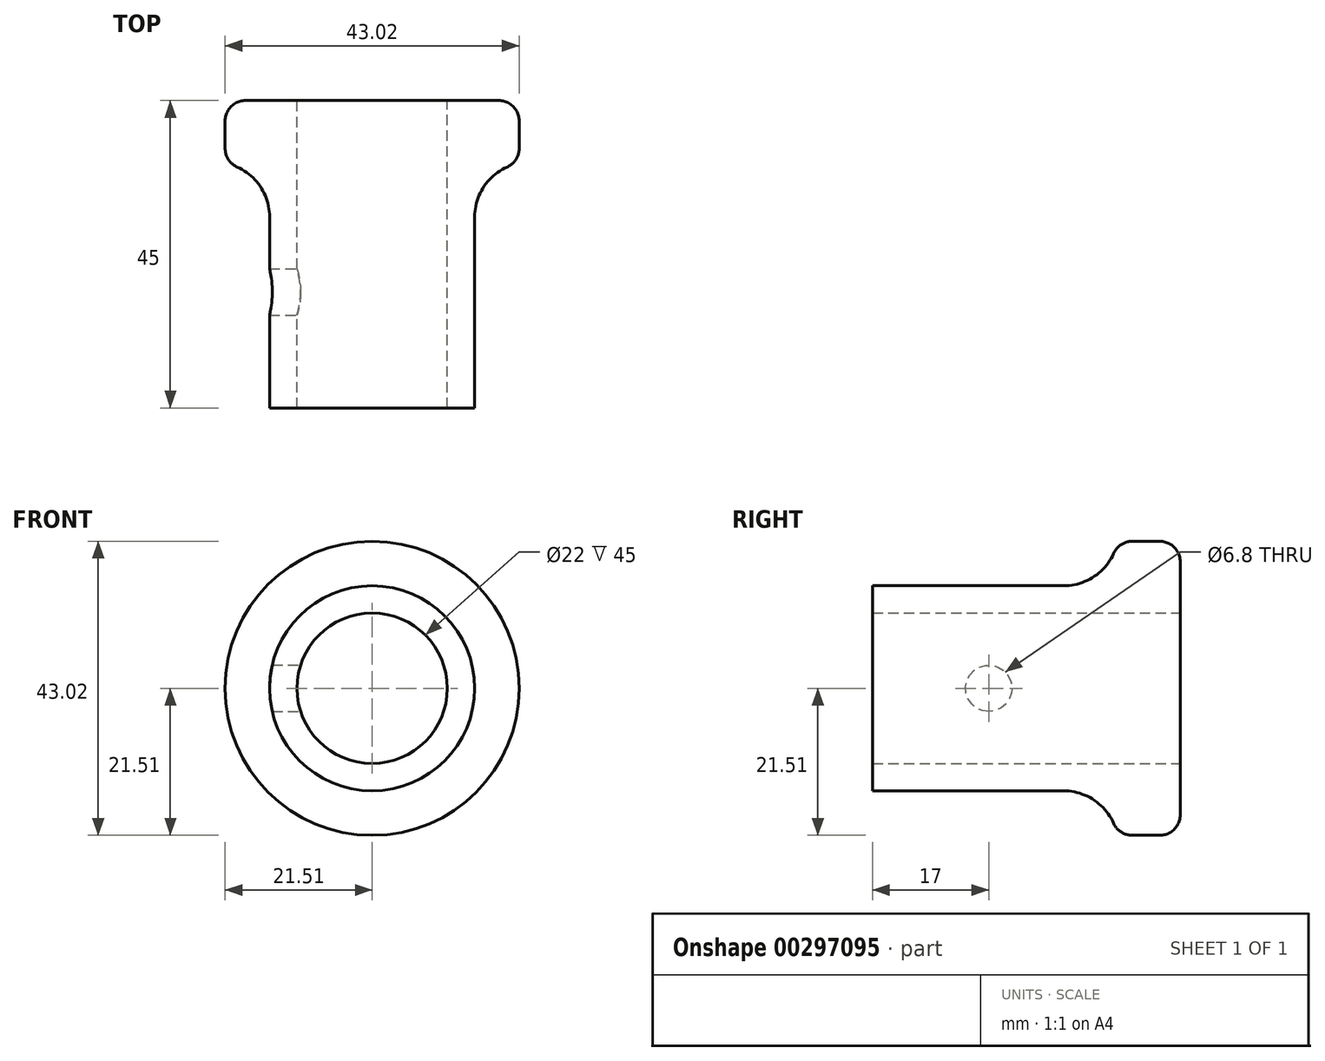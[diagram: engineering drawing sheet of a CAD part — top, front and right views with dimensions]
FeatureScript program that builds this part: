
annotation { "Feature Type Name" : "Feature", "Feature Type Description" : "" }
export const myFeature = defineFeature(function(context is Context, id is Id, definition is map)
    precondition{}
    {
        {
            var Q0;
            Q0=qCreatedBy(makeId("Front.planeOp"),FACE);
            var sketch = newSketch(context, id + "F0", { "sketchPlane" : qUnion([Q0])});
            skCircle(sketch, "E0", {"center": v(0, 0) * mm, "radius": 15 * mm});
            skSolve(sketch);
        }
        {
            var Q0;
            Q0 = qSketchRegion(id + "F0", true);
            extrude(context, id + "F1", {"entities" : qUnion([Q0]), "depth" : 45 * mm});
        }
        {
            var Q0;
            Q0=qCreatedBy(makeId("Front.planeOp"),FACE);
            var sketch = newSketch(context, id + "F2", { "sketchPlane" : qUnion([Q0])});
            skCircle(sketch, "E1", {"center": v(0, 0) * mm, "radius": 21.51 * mm});
            skSolve(sketch);
        }
        {
            var Q0;
            Q0=makeQuery(id+"F2.imprint","IMPRINT",FACE,{"disambiguationData":[TD([[makeQuery(id+"F2.imprint","IMPRINT",EDGE,{"derivedFrom":sQuery(id+"F2.wireOp",EDGE,"E1")}),1.0]])]});
            extrude(context, id + "F3", {"entities" : qUnion([Q0]), "operationType" : NewBodyOperationType.ADD, "depth" : 10 * mm});
        }
        {
            var Q0;
            Q0=sQuery(id+"F0.wireOp",VERTEX,"E0.center");
            var Q1;
            Q1=makeQuery(id+"F1.opExtrude","SWEPT_BODY",BODY,{"disambiguationData":[OSD([sQuery(id+"F0.wireOp",EDGE,"E0")])]});
            hole(context, id + "F4", {"style" : HoleStyle.SIMPLE, "endStyle" : HoleEndStyle.THROUGH, "oppositeDirection" : true, "holeDiameter" : 22 * mm, "tappedDepth" : 12.7 * mm, "tapClearance" : 3, "locations" : qUnion([Q0]), "scope" : qUnion([Q1])});
        }
        {
            var Q0;
            Q0=qCreatedBy(makeId("Right.planeOp"),FACE);
            var sketch = newSketch(context, id + "F5", { "sketchPlane" : qUnion([Q0])});
            skPoint(sketch, "E2", {"position": v(-28, 0) * mm});
            skPoint(sketch, "E3", {"position": v(-28, -20.88) * mm});
            skSolve(sketch);
        }
        {
            var Q0;
            Q0=sQuery(id+"F5.wireOp",VERTEX,"E2");
            var Q1;
            Q1=makeQuery(id+"F1.opExtrude","SWEPT_BODY",BODY,{"disambiguationData":[OSD([sQuery(id+"F0.wireOp",EDGE,"E0")])]});
            hole(context, id + "F6", {"style" : HoleStyle.SIMPLE, "endStyle" : HoleEndStyle.THROUGH, "standardTappedOrClearance" : lookupTablePath({ "standard" : "ISO", "engagement" : "75%", "pitch" : "1.25 mm", "size" : "M8", "type" : "Tapped" }), "standardBlindInLast" : lookupTablePath({ "standard" : "ISO", "engagement" : "75%", "pitch" : "1.25 mm", "size" : "M8", "type" : "Tapped" }), "holeDiameter" : 6.8 * mm, "showTappedDepth" : true, "tappedDepth" : 12 * mm, "tapClearance" : 3, "locations" : qUnion([Q0]), "scope" : qUnion([Q1]), "majorDiameter" : 8 * mm});
        }
        {
            var Q0;
            Q0=makeQuery(id+"F3.opExtrude","SWEPT_FACE",FACE,{"disambiguationData":[OSD([sQuery(id+"F2.wireOp",EDGE,"E1")])]});
            fillet(context, id + "F7", {"entities" : qUnion([Q0]), "radius" : 3 * mm, "tangentPropagation" : true, "allowEdgeOverflow" : false});
        }
        {
            var Q0;
            Q0=makeQuery(id+"F3.boolean.opBoolean","INTERSECT",EDGE,{"derivedFrom":[makeQuery(id+"F1.opExtrude","SWEPT_FACE",FACE,{"disambiguationData":[OSD([sQuery(id+"F0.wireOp",EDGE,"E0")])]}),makeQuery(id+"F3.opExtrude","CAP_FACE",FACE,{"disambiguationData":[OSD([sQuery(id+"F2.wireOp",EDGE,"E1")])],"isStart":false})]});
            fillet(context, id + "F8", {"entities" : qUnion([Q0]), "radius" : 8 * mm, "tangentPropagation" : true, "allowEdgeOverflow" : false});
        }
    });
